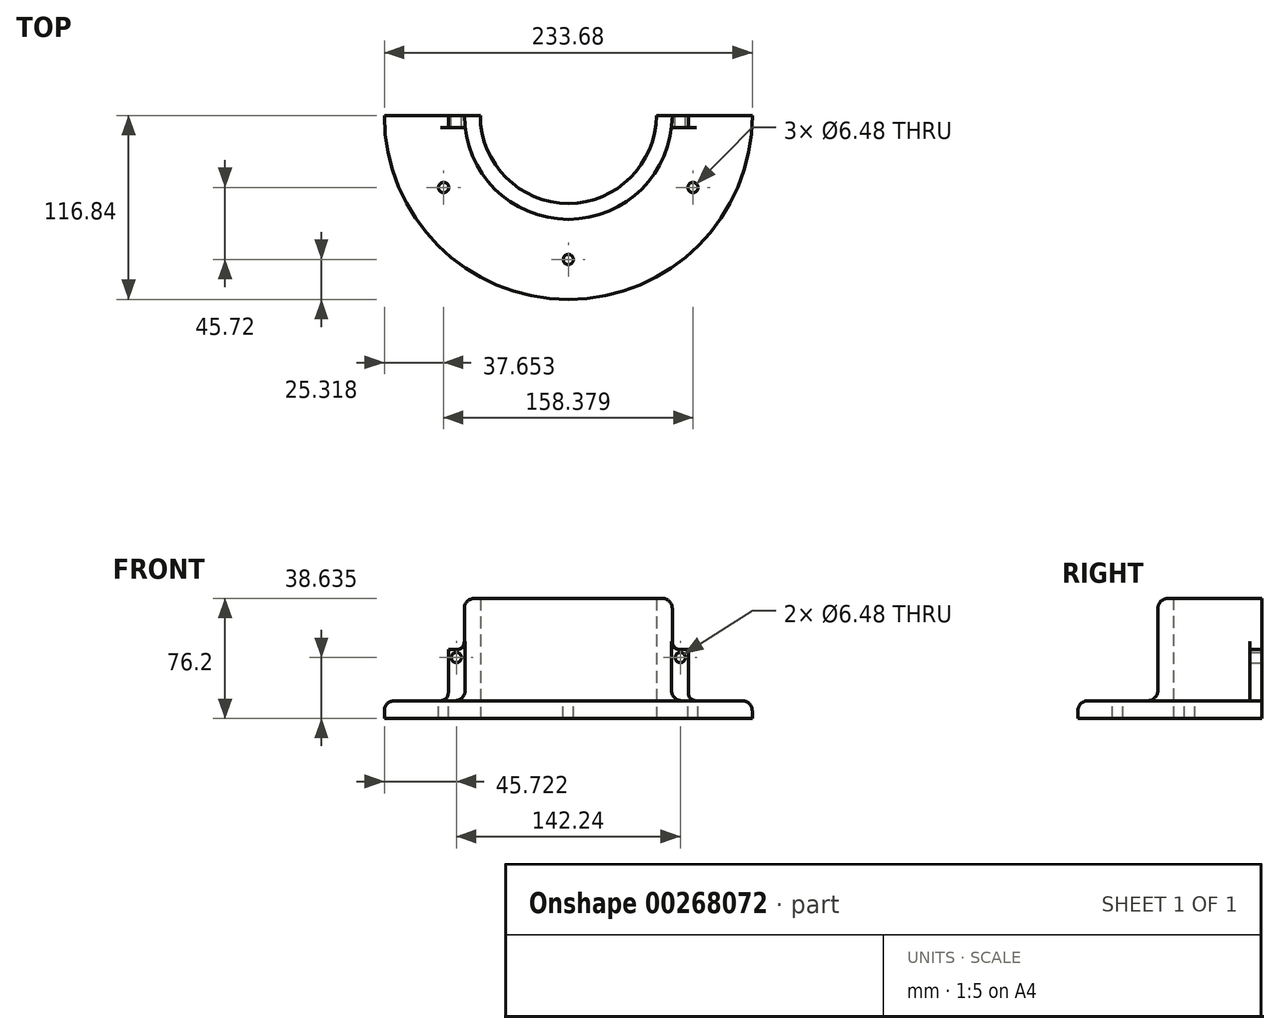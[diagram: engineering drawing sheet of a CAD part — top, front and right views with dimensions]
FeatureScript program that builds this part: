
annotation { "Feature Type Name" : "Feature", "Feature Type Description" : "" }
export const myFeature = defineFeature(function(context is Context, id is Id, definition is map)
    precondition{}
    {
        {
            var Q0;
            Q0=qCreatedBy(makeId("Front.planeOp"),FACE);
            var sketch = newSketch(context, id + "F0", { "sketchPlane" : qUnion([Q0])});
            skLineSegment(sketch, "E0.bottom", {"start": v(-66.28, 68.83) * mm, "end": v(-62.47, 68.83) * mm});
            skLineSegment(sketch, "E0.top", {"start": v(-66.28, -7.37) * mm, "end": v(-56.4, -7.37) * mm});
            skLineSegment(sketch, "E0.left", {"start": v(-66.28, 68.83) * mm, "end": v(-66.28, -7.37) * mm});
            skLineSegment(sketch, "E0.right", {"start": v(-56.12, 62.48) * mm, "end": v(-56.12, 10.2) * mm});
            skLineSegment(sketch, "E1.bottom", {"start": v(-56.4, -7.37) * mm, "end": v(-5.32, -7.37) * mm});
            skLineSegment(sketch, "E1.top", {"start": v(-49.77, 3.86) * mm, "end": v(-11.67, 3.86) * mm});
            skLineSegment(sketch, "E1.left", {"start": v(-56.4, -7.37) * mm, "end": v(-56.4, 3.86) * mm});
            skLineSegment(sketch, "E1.right", {"start": v(-5.32, -7.37) * mm, "end": v(-5.32, -2.5) * mm});
            skLineSegment(sketch, "E2", {"start": v(-122.16, 68.83) * mm, "end": v(-122.16, -7.37) * mm});
            skPoint(sketch, "E3.newPointA", {"position": v(-56.12, -7.37) * mm});
            skPoint(sketch, "E3.newPointB", {"position": v(-56.12, 3.86) * mm});
            skArc(sketch, "E3.filletArc", {"start": v(-56.12, 10.2) * mm, "mid": v(-54.26, 5.72) * mm, "end": v(-49.77, 3.86) * mm});
            skPoint(sketch, "E4.visualSharp", {"position": v(-5.32, 3.86) * mm});
            skArc(sketch, "E4.filletArc", {"start": v(-5.32, -2.5) * mm, "mid": v(-7.18, 2) * mm, "end": v(-11.67, 3.86) * mm});
            skPoint(sketch, "E5.visualSharp", {"position": v(-56.12, 68.83) * mm});
            skArc(sketch, "E5.filletArc", {"start": v(-56.12, 62.48) * mm, "mid": v(-57.98, 66.97) * mm, "end": v(-62.47, 68.83) * mm});
            skSolve(sketch);
        }
        {
            var Q0;
            Q0 = qSketchRegion(id + "F0", true);
            var Q1;
            Q1=sQuery(id+"F0.wireOp",EDGE,"E2");
            revolve(context, id + "F1", {"entities" : qUnion([Q0]), "axis" : qUnion([Q1]), "revolveType" : RevolveType.ONE_DIRECTION, "angle" : 180 * degree});
        }
        {
            var Q0;
            Q0=makeQuery(id+"F1.opRevolve","CAP_FACE",FACE,{"disambiguationData":[OSD([sQuery(id+"F0.wireOp",EDGE,"E0.bottom"),sQuery(id+"F0.wireOp",EDGE,"E0.top"),sQuery(id+"F0.wireOp",EDGE,"E0.left"),sQuery(id+"F0.wireOp",EDGE,"E0.right"),sQuery(id+"F0.wireOp",EDGE,"E1.bottom"),sQuery(id+"F0.wireOp",EDGE,"E1.top"),sQuery(id+"F0.wireOp",EDGE,"E1.right"),sQuery(id+"F0.wireOp",EDGE,"E3.filletArc"),sQuery(id+"F0.wireOp",EDGE,"E4.filletArc"),sQuery(id+"F0.wireOp",EDGE,"E5.filletArc")])],"isStart":true});
            var sketch = newSketch(context, id + "F2", { "sketchPlane" : qUnion([Q0])});
            skPoint(sketch, "E6.firstSnap0", {"position": v(56.12, 36.34) * mm});
            skLineSegment(sketch, "E6.bottom", {"start": v(66.28, 36.34) * mm, "end": v(56.12, 36.34) * mm});
            skLineSegment(sketch, "E6.top", {"start": v(66.28, 26.18) * mm, "end": v(56.12, 26.18) * mm});
            skLineSegment(sketch, "E6.left", {"start": v(66.28, 36.34) * mm, "end": v(66.28, 26.18) * mm});
            skLineSegment(sketch, "E6.right", {"start": v(56.12, 36.34) * mm, "end": v(56.12, 26.18) * mm});
            skLineSegment(sketch, "E7.bottom", {"start": v(56.12, 36.34) * mm, "end": v(56.12, 36.34) * mm});
            skLineSegment(sketch, "E7.top", {"start": v(56.12, 26.18) * mm, "end": v(56.12, 26.18) * mm});
            skLineSegment(sketch, "E8.bottom", {"start": v(56.12, 36.34) * mm, "end": v(45.96, 36.34) * mm});
            skLineSegment(sketch, "E8.top", {"start": v(56.12, 26.18) * mm, "end": v(45.96, 26.18) * mm});
            skLineSegment(sketch, "E8.right", {"start": v(45.96, 36.34) * mm, "end": v(45.96, 26.18) * mm});
            skSolve(sketch);
        }
        {
            var Q0;
            Q0 = qSketchRegion(id + "F2", true);
            extrude(context, id + "F3", {"entities" : qUnion([Q0]), "operationType" : NewBodyOperationType.ADD, "oppositeDirection" : true, "depth" : 7.62 * mm});
        }
        {
            var Q0;
            Q0=makeQuery(id+"F3.boolean.opBoolean","MERGE",FACE,{"derivedFrom":[makeQuery(id+"F1.opRevolve","CAP_FACE",FACE,{"disambiguationData":[OSD([sQuery(id+"F0.wireOp",EDGE,"E0.bottom"),sQuery(id+"F0.wireOp",EDGE,"E0.top"),sQuery(id+"F0.wireOp",EDGE,"E0.left"),sQuery(id+"F0.wireOp",EDGE,"E0.right"),sQuery(id+"F0.wireOp",EDGE,"E1.bottom"),sQuery(id+"F0.wireOp",EDGE,"E1.top"),sQuery(id+"F0.wireOp",EDGE,"E1.right"),sQuery(id+"F0.wireOp",EDGE,"E3.filletArc"),sQuery(id+"F0.wireOp",EDGE,"E4.filletArc"),sQuery(id+"F0.wireOp",EDGE,"E5.filletArc")])],"isStart":true}),makeQuery(id+"F3.opExtrude","CAP_FACE",FACE,{"disambiguationData":[OSD([sQuery(id+"F2.wireOp",EDGE,"E6.bottom"),sQuery(id+"F2.wireOp",EDGE,"E6.top"),sQuery(id+"F2.wireOp",EDGE,"E6.left"),sQuery(id+"F2.wireOp",EDGE,"E8.bottom"),sQuery(id+"F2.wireOp",EDGE,"E8.top"),sQuery(id+"F2.wireOp",EDGE,"E8.right")])],"isStart":true})]});
            var sketch = newSketch(context, id + "F4", { "sketchPlane" : qUnion([Q0])});
            skCircle(sketch, "E9", {"center": v(51.04, 31.26) * mm, "radius": 3.24 * mm});
            skPoint(sketch, "E9.centerSnap0", {"position": v(45.96, 31.26) * mm});
            skPoint(sketch, "E9.centerSnap1", {"position": v(51.04, 36.34) * mm});
            skSolve(sketch);
        }
        {
            var Q0;
            Q0 = qSketchRegion(id + "F4", true);
            extrude(context, id + "F5", {"entities" : qUnion([Q0]), "operationType" : NewBodyOperationType.REMOVE, "oppositeDirection" : true, "depth" : 25.4 * mm});
        }
        {
            var Q0;
            Q0=makeQuery(id+"F1.opRevolve","CAP_FACE",FACE,{"disambiguationData":[OSD([sQuery(id+"F0.wireOp",EDGE,"E0.bottom"),sQuery(id+"F0.wireOp",EDGE,"E0.top"),sQuery(id+"F0.wireOp",EDGE,"E0.left"),sQuery(id+"F0.wireOp",EDGE,"E0.right"),sQuery(id+"F0.wireOp",EDGE,"E1.bottom"),sQuery(id+"F0.wireOp",EDGE,"E1.top"),sQuery(id+"F0.wireOp",EDGE,"E1.right"),sQuery(id+"F0.wireOp",EDGE,"E3.filletArc"),sQuery(id+"F0.wireOp",EDGE,"E4.filletArc"),sQuery(id+"F0.wireOp",EDGE,"E5.filletArc")])],"isStart":false});
            var sketch = newSketch(context, id + "F6", { "sketchPlane" : qUnion([Q0])});
            skLineSegment(sketch, "E10.bottom", {"start": v(188.2, 36.34) * mm, "end": v(178.04, 36.34) * mm});
            skLineSegment(sketch, "E10.top", {"start": v(188.2, 26.18) * mm, "end": v(178.04, 26.18) * mm});
            skLineSegment(sketch, "E10.left", {"start": v(188.2, 36.34) * mm, "end": v(188.2, 26.18) * mm});
            skLineSegment(sketch, "E10.right", {"start": v(178.04, 36.34) * mm, "end": v(178.04, 26.18) * mm});
            skLineSegment(sketch, "E11.bottom", {"start": v(188.2, 36.34) * mm, "end": v(198.36, 36.34) * mm});
            skLineSegment(sketch, "E11.top", {"start": v(188.2, 26.18) * mm, "end": v(198.36, 26.18) * mm});
            skLineSegment(sketch, "E11.right", {"start": v(198.36, 36.34) * mm, "end": v(198.36, 26.18) * mm});
            skSolve(sketch);
        }
        {
            var Q0;
            Q0 = qSketchRegion(id + "F6", true);
            extrude(context, id + "F7", {"entities" : qUnion([Q0]), "operationType" : NewBodyOperationType.ADD, "oppositeDirection" : true, "depth" : 7.62 * mm});
        }
        {
            var Q0;
            Q0=makeQuery(id+"F7.boolean.opBoolean","MERGE",FACE,{"derivedFrom":[makeQuery(id+"F1.opRevolve","CAP_FACE",FACE,{"disambiguationData":[OSD([sQuery(id+"F0.wireOp",EDGE,"E0.bottom"),sQuery(id+"F0.wireOp",EDGE,"E0.top"),sQuery(id+"F0.wireOp",EDGE,"E0.left"),sQuery(id+"F0.wireOp",EDGE,"E0.right"),sQuery(id+"F0.wireOp",EDGE,"E1.bottom"),sQuery(id+"F0.wireOp",EDGE,"E1.top"),sQuery(id+"F0.wireOp",EDGE,"E1.right"),sQuery(id+"F0.wireOp",EDGE,"E3.filletArc"),sQuery(id+"F0.wireOp",EDGE,"E4.filletArc"),sQuery(id+"F0.wireOp",EDGE,"E5.filletArc")])],"isStart":false}),makeQuery(id+"F7.opExtrude","CAP_FACE",FACE,{"disambiguationData":[OSD([sQuery(id+"F6.wireOp",EDGE,"E10.bottom"),sQuery(id+"F6.wireOp",EDGE,"E10.top"),sQuery(id+"F6.wireOp",EDGE,"E10.right"),sQuery(id+"F6.wireOp",EDGE,"E11.bottom"),sQuery(id+"F6.wireOp",EDGE,"E11.top"),sQuery(id+"F6.wireOp",EDGE,"E11.right")])],"isStart":true})]});
            var sketch = newSketch(context, id + "F8", { "sketchPlane" : qUnion([Q0])});
            skCircle(sketch, "E12", {"center": v(193.28, 31.26) * mm, "radius": 3.24 * mm});
            skPoint(sketch, "E12.centerSnap0", {"position": v(198.36, 31.26) * mm});
            skPoint(sketch, "E12.centerSnap1", {"position": v(193.28, 36.34) * mm});
            skSolve(sketch);
        }
        {
            var Q0;
            Q0 = qSketchRegion(id + "F8", true);
            extrude(context, id + "F9", {"entities" : qUnion([Q0]), "operationType" : NewBodyOperationType.REMOVE, "oppositeDirection" : true, "depth" : 25.4 * mm});
        }
        {
            var Q0;
            Q0=makeQuery(id+"F1.opRevolve","SWEPT_FACE",FACE,{"disambiguationData":[OSD([sQuery(id+"F0.wireOp",EDGE,"E1.top")])]});
            var sketch = newSketch(context, id + "F10", { "sketchPlane" : qUnion([Q0])});
            skLineSegment(sketch, "E13", {"start": v(-213.6, 0) * mm, "end": v(-30.72, 0) * mm});
            skArc(sketch, "E14", {"start": v(-213.6, 0) * mm, "mid": v(-122.16, -91.52) * mm, "end": v(-30.72, 0) * mm});
            skLineSegment(sketch, "E15", {"start": v(-122.16, -0.08) * mm, "end": v(-201.35, -45.8) * mm});
            skLineSegment(sketch, "E16", {"start": v(-122.16, -0.08) * mm, "end": v(-122.16, -91.52) * mm});
            skLineSegment(sketch, "E17", {"start": v(-122.16, -0.08) * mm, "end": v(-42.97, -45.8) * mm});
            skCircle(sketch, "E18", {"center": v(-201.35, -45.8) * mm, "radius": 3.24 * mm});
            skCircle(sketch, "E19", {"center": v(-122.16, -91.52) * mm, "radius": 3.24 * mm});
            skCircle(sketch, "E20", {"center": v(-42.97, -45.8) * mm, "radius": 3.24 * mm});
            skSolve(sketch);
        }
        {
            var Q0;
            {var subQ0=sQuery(id+"F10.wireOp",EDGE,"E14");var subQ1=makeQuery(id+"F10.imprint","INTERSECT",VERTEX,{"derivedFrom":[subQ0,sQuery(id+"F10.wireOp",EDGE,"E15")]});Q0=makeQuery(id+"F10.imprint","IMPRINT",FACE,{"disambiguationData":[TD([[makeQuery(id+"F10.imprint","IMPRINT",EDGE,{"disambiguationData":[TD([[subQ1,1.0]])],"derivedFrom":subQ0}),-1.0]])]});}
            var Q1;
            {var subQ0=sQuery(id+"F10.wireOp",EDGE,"E15");var subQ1=sQuery(id+"F10.wireOp",EDGE,"E14");var subQ2=makeQuery(id+"F10.imprint","INTERSECT",VERTEX,{"derivedFrom":[subQ1,subQ0]});Q1=makeQuery(id+"F10.imprint","IMPRINT",FACE,{"disambiguationData":[TD([[makeQuery(id+"F10.imprint","IMPRINT",EDGE,{"disambiguationData":[TD([[subQ2,1.0]])],"derivedFrom":subQ1}),1.0]])]});}
            var Q2;
            {var subQ0=sQuery(id+"F10.wireOp",EDGE,"E15");var subQ1=sQuery(id+"F10.wireOp",EDGE,"E14");var subQ2=makeQuery(id+"F10.imprint","INTERSECT",VERTEX,{"derivedFrom":[subQ1,subQ0]});Q2=makeQuery(id+"F10.imprint","IMPRINT",FACE,{"disambiguationData":[TD([[makeQuery(id+"F10.imprint","IMPRINT",EDGE,{"disambiguationData":[TD([[subQ2,-1.0]])],"derivedFrom":subQ1}),1.0]])]});}
            var Q3;
            {var subQ0=sQuery(id+"F10.wireOp",EDGE,"E14");var subQ1=makeQuery(id+"F10.imprint","INTERSECT",VERTEX,{"derivedFrom":[subQ0,sQuery(id+"F10.wireOp",EDGE,"E16")]});Q3=makeQuery(id+"F10.imprint","IMPRINT",FACE,{"disambiguationData":[TD([[makeQuery(id+"F10.imprint","IMPRINT",EDGE,{"disambiguationData":[TD([[subQ1,1.0]])],"derivedFrom":subQ0}),-1.0]])]});}
            var Q4;
            {var subQ0=sQuery(id+"F10.wireOp",EDGE,"E16");var subQ1=sQuery(id+"F10.wireOp",EDGE,"E14");var subQ2=makeQuery(id+"F10.imprint","INTERSECT",VERTEX,{"derivedFrom":[subQ1,subQ0]});Q4=makeQuery(id+"F10.imprint","IMPRINT",FACE,{"disambiguationData":[TD([[makeQuery(id+"F10.imprint","IMPRINT",EDGE,{"disambiguationData":[TD([[subQ2,1.0]])],"derivedFrom":subQ1}),1.0]])]});}
            var Q5;
            {var subQ0=sQuery(id+"F10.wireOp",EDGE,"E16");var subQ1=sQuery(id+"F10.wireOp",EDGE,"E14");var subQ2=makeQuery(id+"F10.imprint","INTERSECT",VERTEX,{"derivedFrom":[subQ1,subQ0]});Q5=makeQuery(id+"F10.imprint","IMPRINT",FACE,{"disambiguationData":[TD([[makeQuery(id+"F10.imprint","IMPRINT",EDGE,{"disambiguationData":[TD([[subQ2,-1.0]])],"derivedFrom":subQ1}),1.0]])]});}
            var Q6;
            {var subQ0=sQuery(id+"F10.wireOp",EDGE,"E14");var subQ1=makeQuery(id+"F10.imprint","INTERSECT",VERTEX,{"derivedFrom":[subQ0,sQuery(id+"F10.wireOp",EDGE,"E17")]});Q6=makeQuery(id+"F10.imprint","IMPRINT",FACE,{"disambiguationData":[TD([[makeQuery(id+"F10.imprint","IMPRINT",EDGE,{"disambiguationData":[TD([[subQ1,1.0]])],"derivedFrom":subQ0}),-1.0]])]});}
            var Q7;
            {var subQ0=sQuery(id+"F10.wireOp",EDGE,"E17");var subQ1=sQuery(id+"F10.wireOp",EDGE,"E14");var subQ2=makeQuery(id+"F10.imprint","INTERSECT",VERTEX,{"derivedFrom":[subQ1,subQ0]});Q7=makeQuery(id+"F10.imprint","IMPRINT",FACE,{"disambiguationData":[TD([[makeQuery(id+"F10.imprint","IMPRINT",EDGE,{"disambiguationData":[TD([[subQ2,1.0]])],"derivedFrom":subQ1}),1.0]])]});}
            var Q8;
            {var subQ0=sQuery(id+"F10.wireOp",EDGE,"E17");var subQ1=sQuery(id+"F10.wireOp",EDGE,"E14");var subQ2=makeQuery(id+"F10.imprint","INTERSECT",VERTEX,{"derivedFrom":[subQ1,subQ0]});Q8=makeQuery(id+"F10.imprint","IMPRINT",FACE,{"disambiguationData":[TD([[makeQuery(id+"F10.imprint","IMPRINT",EDGE,{"disambiguationData":[TD([[subQ2,-1.0]])],"derivedFrom":subQ1}),1.0]])]});}
            extrude(context, id + "F11", {"entities" : qUnion([Q0, Q1, Q2, Q3, Q4, Q5, Q6, Q7, Q8]), "operationType" : NewBodyOperationType.REMOVE, "oppositeDirection" : true, "depth" : 25.4 * mm});
        }
        {
            var Q0;
            Q0=makeQuery(id+"F7.opExtrude","SWEPT_FACE",FACE,{"disambiguationData":[OSD([sQuery(id+"F6.wireOp",EDGE,"E10.top"),sQuery(id+"F6.wireOp",EDGE,"E11.top")])]});
            extrude(context, id + "F12", {"entities" : qUnion([Q0]), "operationType" : NewBodyOperationType.ADD, "depth" : 25.4 * mm});
        }
        {
            var Q0;
            Q0=makeQuery(id+"F3.opExtrude","SWEPT_FACE",FACE,{"disambiguationData":[OSD([sQuery(id+"F2.wireOp",EDGE,"E6.top"),sQuery(id+"F2.wireOp",EDGE,"E8.top")])]});
            extrude(context, id + "F13", {"entities" : qUnion([Q0]), "operationType" : NewBodyOperationType.ADD, "depth" : 25.4 * mm});
        }
        {
            var Q0;
            Q0=makeQuery(id+"F12.boolean.opBoolean","INTERSECT",EDGE,{"derivedFrom":[makeQuery(id+"F1.opRevolve","SWEPT_FACE",FACE,{"disambiguationData":[OSD([sQuery(id+"F0.wireOp",EDGE,"E1.top")])]}),makeQuery(id+"F12.opExtrude","SWEPT_FACE",FACE,{"disambiguationData":[OSD([sQuery(id+"F6.wireOp",EDGE,"E11.top"),sQuery(id+"F6.wireOp",EDGE,"E11.right")])]})]});
            var Q1;
            Q1=makeQuery(id+"F7.boolean.opBoolean","INTERSECT",EDGE,{"derivedFrom":[makeQuery(id+"F1.opRevolve","SWEPT_FACE",FACE,{"disambiguationData":[OSD([sQuery(id+"F0.wireOp",EDGE,"E0.right")])]}),makeQuery(id+"F7.opExtrude","SWEPT_FACE",FACE,{"disambiguationData":[OSD([sQuery(id+"F6.wireOp",EDGE,"E10.bottom"),sQuery(id+"F6.wireOp",EDGE,"E11.bottom")])]})]});
            var Q2;
            Q2=makeQuery(id+"F13.boolean.opBoolean","INTERSECT",EDGE,{"derivedFrom":[makeQuery(id+"F1.opRevolve","SWEPT_FACE",FACE,{"disambiguationData":[OSD([sQuery(id+"F0.wireOp",EDGE,"E1.top")])]}),makeQuery(id+"F13.opExtrude","SWEPT_FACE",FACE,{"disambiguationData":[OSD([sQuery(id+"F2.wireOp",EDGE,"E8.top"),sQuery(id+"F2.wireOp",EDGE,"E8.right")])]})]});
            var Q3;
            Q3=makeQuery(id+"F3.boolean.opBoolean","INTERSECT",EDGE,{"derivedFrom":[makeQuery(id+"F1.opRevolve","SWEPT_FACE",FACE,{"disambiguationData":[OSD([sQuery(id+"F0.wireOp",EDGE,"E0.right")])]}),makeQuery(id+"F3.opExtrude","SWEPT_FACE",FACE,{"disambiguationData":[OSD([sQuery(id+"F2.wireOp",EDGE,"E6.bottom"),sQuery(id+"F2.wireOp",EDGE,"E8.bottom")])]})]});
            fillet(context, id + "F14", {"entities" : qUnion([Q0, Q1, Q2, Q3]), "radius" : 5.08 * mm, "tangentPropagation" : true, "allowEdgeOverflow" : false});
        }
    });
